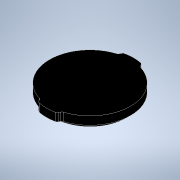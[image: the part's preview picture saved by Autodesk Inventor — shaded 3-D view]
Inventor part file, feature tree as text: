
AUTODESK INVENTOR PART (.ipt)
format: ipt  version: 2022 (Build 260153000, 153)  size: 173,056 bytes
history: native  units: in
note: dims shown in document units (in); Inventor stores cm internally (conversion verified against a paired STEP export)
features: sketch x4, extrude x3, fillet x2, pattern_circular x1, revolve x1
ambient origin geometry x8: Origin, YZ Plane, XZ Plane, XY Plane, X Axis, Y Axis, Z Axis, Center Point
bodies: Solid1 (feature_tree)
feature tree (11):
  extrude  "Extrusion1"  Depth=0.1181in TaperAngle=0.0deg
  extrude  "Extrusion2"  Depth=0.2283in TaperAngle=0.0deg
  extrude  "Extrusion4"  Depth=0.3937in
  fillet  "Fillet2"  Radius=0.6299in
  pattern_circular  "Circular Pattern1"  [2 undecoded]
  revolve  "Revolution1"  [1 undecoded]
  fillet  "Fillet3"  [1 undecoded]
  sketch  "Sketch1"  dims[d0=2.0256in d1=0.1181in d2=0.0in]
  sketch  "Sketch2"  dims[d3=2.2677in d4=0.2283in d5=0.0in]
  sketch  "Sketch5"  dims[d28=0.3937in d29=0.0in d30=0.0787in d33=0.6299in]
  sketch  "Sketch6"  dims[d34=1.0892in d35=1.0892in d36=0.1181in d37=120.0deg d38=0.1181in d39=60.0deg d40=1.1339in d41=0.7874in d42=360.0deg d44=0.1211in d45=0.0787in d46=0.0394in d47=0.086in d48=0.086in d49=0.0197in]
note: 4 required parameter values undecoded (feature->parameter linkage not recoverable at this tier; creation-order binding heuristic only, values carry confidence <= 0.55)